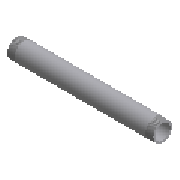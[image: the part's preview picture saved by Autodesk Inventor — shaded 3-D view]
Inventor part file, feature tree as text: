
AUTODESK INVENTOR PART (.ipt)
format: ipt  version: 2013 SP2 (Build 170200200, 200)  size: 148,992 bytes
history: native  units: mm (DEFAULTED — no unit token found)
features: other x6, revolve x1, sketch x1
ambient origin geometry x8: Origin, YZ Plane, XZ Plane, XY Plane, X Axis, Y Axis, Z Axis, Center Point
bodies: Solid1 (feature_tree)
feature tree (8):
  revolve  "Revolution1"  [1 undecoded]
  other  "Work Axis1"
  other  "Work Point5"
  other  "Work Axis2"
  other  "Work Point6"
  other  "Work Axis3"
  other  "Work Axis4"
  sketch  "Sketch1"  dims[d0=33.401mm d1=0.312398mm d2=26.6446mm d3=154.0002mm d28=90.0deg d4=17.34312mm d30=25.4mm d31=0.0mm d32=25.4mm d33=0.0mm d5=33.677098mm]
note: 1 required parameter value undecoded (feature->parameter linkage not recoverable at this tier; creation-order binding heuristic only, values carry confidence <= 0.55)
